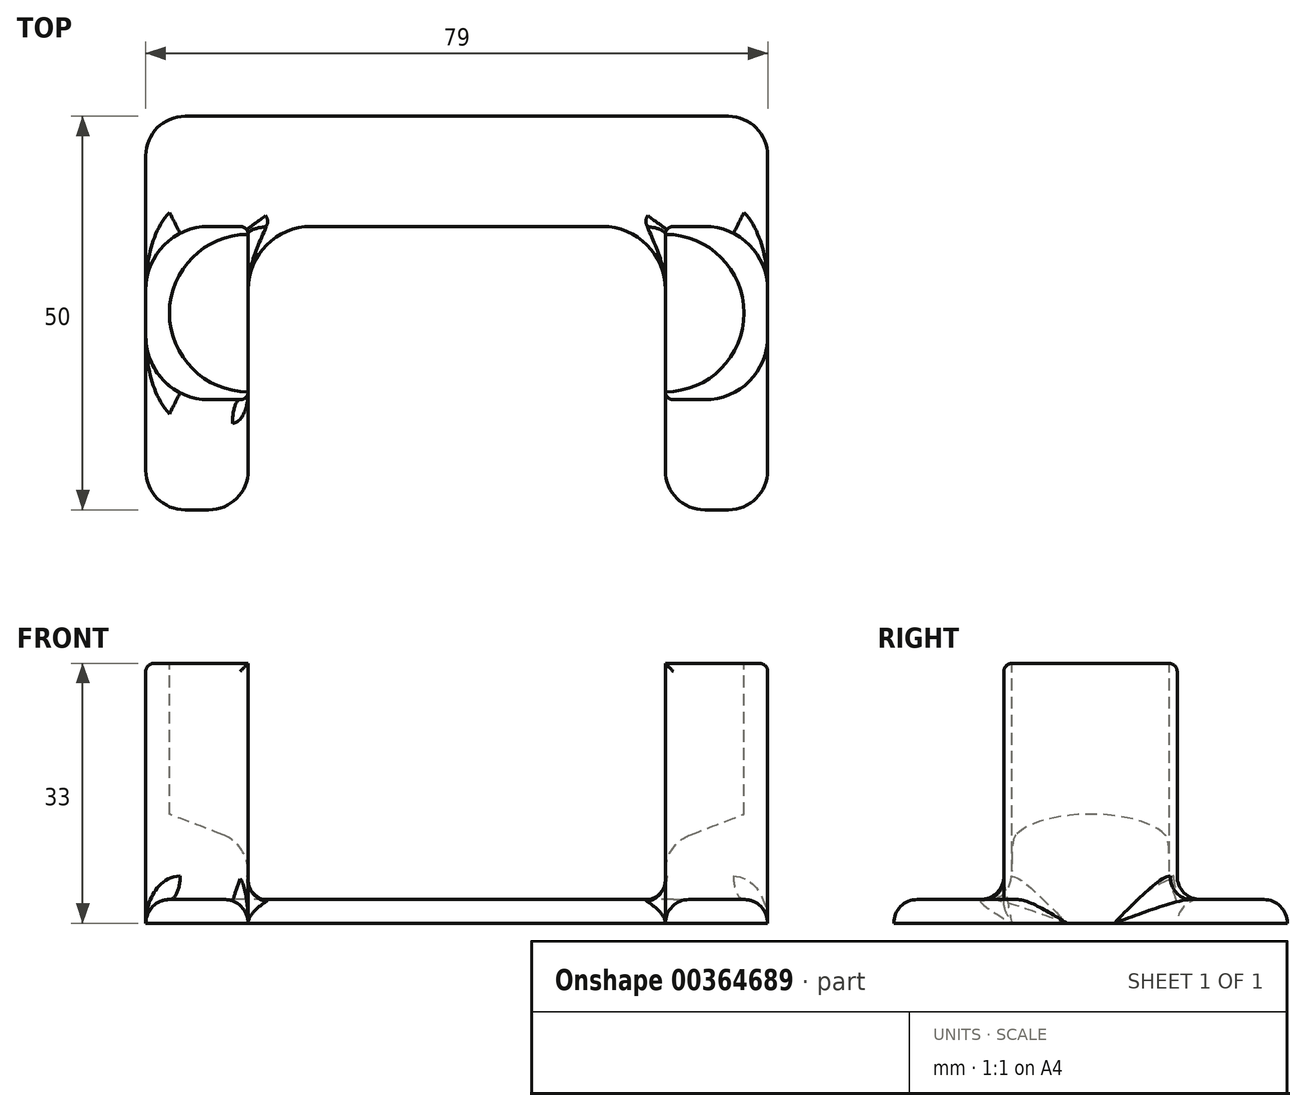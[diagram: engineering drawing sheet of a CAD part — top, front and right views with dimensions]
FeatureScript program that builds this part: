
annotation { "Feature Type Name" : "Feature", "Feature Type Description" : "" }
export const myFeature = defineFeature(function(context is Context, id is Id, definition is map)
    precondition{}
    {
        {
            var Q0;
            Q0=qCreatedBy(makeId("Top.planeOp"),FACE);
            var sketch = newSketch(context, id + "F0", { "sketchPlane" : qUnion([Q0])});
            skLineSegment(sketch, "E0", {"start": v(-45.81, 54.11) * mm, "end": v(33.19, 54.11) * mm});
            skLineSegment(sketch, "E1", {"start": v(33.19, 54.11) * mm, "end": v(33.19, 4.11) * mm});
            skLineSegment(sketch, "E2", {"start": v(33.19, 4.11) * mm, "end": v(20.19, 4.11) * mm});
            skLineSegment(sketch, "E3", {"start": v(20.19, 4.11) * mm, "end": v(20.19, 40.11) * mm});
            skLineSegment(sketch, "E4", {"start": v(20.19, 40.11) * mm, "end": v(-32.81, 40.11) * mm});
            skLineSegment(sketch, "E5", {"start": v(-32.81, 40.11) * mm, "end": v(-32.81, 4.11) * mm});
            skLineSegment(sketch, "E6", {"start": v(-32.81, 4.11) * mm, "end": v(-45.81, 4.11) * mm});
            skLineSegment(sketch, "E7", {"start": v(-45.81, 4.11) * mm, "end": v(-45.81, 54.11) * mm});
            skSolve(sketch);
        }
        {
            var Q0;
            Q0=makeQuery(id+"F0.imprint","IMPRINT",FACE,{"disambiguationData":[TD([[makeQuery(id+"F0.imprint","IMPRINT",EDGE,{"derivedFrom":sQuery(id+"F0.wireOp",EDGE,"E0")}),-1.0]])]});
            extrude(context, id + "F1", {"entities" : qUnion([Q0]), "depth" : 3 * mm});
        }
        {
            var Q0;
            Q0=makeQuery(id+"F1.opExtrude","CAP_FACE",FACE,{"disambiguationData":[OSD([sQuery(id+"F0.wireOp",EDGE,"E0"),sQuery(id+"F0.wireOp",EDGE,"E1"),sQuery(id+"F0.wireOp",EDGE,"E2"),sQuery(id+"F0.wireOp",EDGE,"E3"),sQuery(id+"F0.wireOp",EDGE,"E4"),sQuery(id+"F0.wireOp",EDGE,"E5"),sQuery(id+"F0.wireOp",EDGE,"E6"),sQuery(id+"F0.wireOp",EDGE,"E7")])],"isStart":false});
            var sketch = newSketch(context, id + "F2", { "sketchPlane" : qUnion([Q0])});
            skLineSegment(sketch, "E8.bottom", {"start": v(-32.81, 40.11) * mm, "end": v(-45.81, 40.11) * mm});
            skLineSegment(sketch, "E8.top", {"start": v(-32.81, 18.11) * mm, "end": v(-45.81, 18.11) * mm});
            skLineSegment(sketch, "E8.left", {"start": v(-32.81, 40.11) * mm, "end": v(-32.81, 18.11) * mm});
            skLineSegment(sketch, "E8.right", {"start": v(-45.81, 40.11) * mm, "end": v(-45.81, 18.11) * mm});
            skLineSegment(sketch, "E9.bottom", {"start": v(20.19, 40.11) * mm, "end": v(33.19, 40.11) * mm});
            skLineSegment(sketch, "E9.top", {"start": v(20.19, 18.11) * mm, "end": v(33.19, 18.11) * mm});
            skLineSegment(sketch, "E9.left", {"start": v(20.19, 40.11) * mm, "end": v(20.19, 18.11) * mm});
            skLineSegment(sketch, "E9.right", {"start": v(33.19, 40.11) * mm, "end": v(33.19, 18.11) * mm});
            skSolve(sketch);
        }
        {
            var Q0;
            Q0=makeQuery(id+"F2.imprint","IMPRINT",FACE,{"disambiguationData":[TD([[makeQuery(id+"F2.imprint","IMPRINT",EDGE,{"derivedFrom":sQuery(id+"F2.wireOp",EDGE,"E8.bottom")}),1.0]])]});
            var Q1;
            Q1=makeQuery(id+"F2.imprint","IMPRINT",FACE,{"disambiguationData":[TD([[makeQuery(id+"F2.imprint","IMPRINT",EDGE,{"derivedFrom":sQuery(id+"F2.wireOp",EDGE,"E9.bottom")}),-1.0]])]});
            extrude(context, id + "F3", {"entities" : qUnion([Q0, Q1]), "operationType" : NewBodyOperationType.ADD, "depth" : 30 * mm});
        }
        {
            var Q0;
            Q0=makeQuery(id+"F3.opExtrude","CAP_FACE",FACE,{"disambiguationData":[OSD([sQuery(id+"F2.wireOp",EDGE,"E8.bottom"),sQuery(id+"F2.wireOp",EDGE,"E8.top"),sQuery(id+"F2.wireOp",EDGE,"E8.left"),sQuery(id+"F2.wireOp",EDGE,"E8.right")])],"isStart":false});
            var sketch = newSketch(context, id + "F4", { "sketchPlane" : qUnion([Q0])});
            skCircle(sketch, "E10", {"center": v(-32.81, 29.11) * mm, "radius": 10 * mm});
            skSolve(sketch);
        }
        {
            var Q0;
            {var subQ0=sQuery(id+"F4.wireOp",EDGE,"E10");var subQ1=makeQuery(id+"F3.opExtrude","CAP_EDGE",EDGE,{"disambiguationData":[OSD([sQuery(id+"F2.wireOp",EDGE,"E8.left")])],"isStart":false});var subQ2=makeQuery(id+"F4.imprint","INTERSECT",VERTEX,{"disambiguationData":[OD(0.0)],"derivedFrom":[subQ1,subQ0]});Q0=makeQuery(id+"F4.imprint","IMPRINT",FACE,{"disambiguationData":[TD([[makeQuery(id+"F4.imprint","IMPRINT",EDGE,{"disambiguationData":[TD([[subQ2,-1.0]])],"derivedFrom":subQ0}),1.0]])]});}
            extrude(context, id + "F5", {"entities" : qUnion([Q0]), "operationType" : NewBodyOperationType.REMOVE, "oppositeDirection" : true, "depth" : 30 * mm});
        }
        {
            var Q0;
            Q0=makeQuery(id+"F3.opExtrude","CAP_FACE",FACE,{"disambiguationData":[OSD([sQuery(id+"F2.wireOp",EDGE,"E9.bottom"),sQuery(id+"F2.wireOp",EDGE,"E9.top"),sQuery(id+"F2.wireOp",EDGE,"E9.left"),sQuery(id+"F2.wireOp",EDGE,"E9.right")])],"isStart":false});
            var sketch = newSketch(context, id + "F6", { "sketchPlane" : qUnion([Q0])});
            skCircle(sketch, "E11", {"center": v(20.19, 29.11) * mm, "radius": 10 * mm});
            skSolve(sketch);
        }
        {
            var Q0;
            {var subQ0=sQuery(id+"F6.wireOp",EDGE,"E11");var subQ1=makeQuery(id+"F3.opExtrude","CAP_EDGE",EDGE,{"disambiguationData":[OSD([sQuery(id+"F2.wireOp",EDGE,"E9.left")])],"isStart":false});var subQ2=makeQuery(id+"F6.imprint","INTERSECT",VERTEX,{"disambiguationData":[OD(0.0)],"derivedFrom":[subQ1,subQ0]});Q0=makeQuery(id+"F6.imprint","IMPRINT",FACE,{"disambiguationData":[TD([[makeQuery(id+"F6.imprint","IMPRINT",EDGE,{"disambiguationData":[TD([[subQ2,1.0]])],"derivedFrom":subQ0}),1.0]])]});}
            extrude(context, id + "F7", {"entities" : qUnion([Q0]), "operationType" : NewBodyOperationType.REMOVE, "oppositeDirection" : true, "depth" : 30 * mm});
        }
        {
            var Q0;
            Q0=makeQuery(id+"F3.opExtrude","SWEPT_FACE",FACE,{"disambiguationData":[OSD([sQuery(id+"F2.wireOp",EDGE,"E8.top")])]});
            var sketch = newSketch(context, id + "F8", { "sketchPlane" : qUnion([Q0])});
            skLineSegment(sketch, "E12", {"start": v(-45.81, 3) * mm, "end": v(-45.81, 15) * mm});
            skLineSegment(sketch, "E13", {"start": v(-45.81, 15) * mm, "end": v(-32.81, 10) * mm});
            skLineSegment(sketch, "E14", {"start": v(-32.81, 10) * mm, "end": v(-32.81, 3) * mm});
            skLineSegment(sketch, "E15", {"start": v(-32.81, 3) * mm, "end": v(-45.81, 3) * mm});
            skSolve(sketch);
        }
        {
            var Q0;
            Q0=makeQuery(id+"F8.imprint","IMPRINT",FACE,{"disambiguationData":[TD([[makeQuery(id+"F8.imprint","IMPRINT",EDGE,{"derivedFrom":sQuery(id+"F8.wireOp",EDGE,"E12")}),1.0]])]});
            extrude(context, id + "F9", {"entities" : qUnion([Q0]), "operationType" : NewBodyOperationType.ADD, "depth" : -22 * mm});
        }
        {
            var Q0;
            Q0=makeQuery(id+"F3.opExtrude","SWEPT_FACE",FACE,{"disambiguationData":[OSD([sQuery(id+"F2.wireOp",EDGE,"E9.top")])]});
            var sketch = newSketch(context, id + "F10", { "sketchPlane" : qUnion([Q0])});
            skLineSegment(sketch, "E16", {"start": v(20.19, 3) * mm, "end": v(20.19, 10) * mm});
            skLineSegment(sketch, "E17", {"start": v(20.19, 10) * mm, "end": v(33.19, 15) * mm});
            skLineSegment(sketch, "E18", {"start": v(33.19, 15) * mm, "end": v(33.19, 3) * mm});
            skLineSegment(sketch, "E19", {"start": v(33.19, 3) * mm, "end": v(20.19, 3) * mm});
            skSolve(sketch);
        }
        {
            var Q0;
            Q0=makeQuery(id+"F10.imprint","IMPRINT",FACE,{"disambiguationData":[TD([[makeQuery(id+"F10.imprint","IMPRINT",EDGE,{"derivedFrom":sQuery(id+"F10.wireOp",EDGE,"E16")}),1.0]])]});
            extrude(context, id + "F11", {"entities" : qUnion([Q0]), "operationType" : NewBodyOperationType.ADD, "depth" : -22 * mm});
        }
        {
            var Q0;
            Q0=makeQuery(id+"F3.opExtrude","SWEPT_EDGE",EDGE,{"disambiguationData":[OSD([sQuery(id+"F0.wireOp",EDGE,"E1"),sQuery(id+"F2.wireOp",EDGE,"E9.top"),sQuery(id+"F2.wireOp",EDGE,"E9.right")])]});
            var Q1;
            Q1=makeQuery(id+"F3.opExtrude","SWEPT_EDGE",EDGE,{"disambiguationData":[OSD([sQuery(id+"F0.wireOp",EDGE,"E1"),sQuery(id+"F2.wireOp",EDGE,"E9.bottom"),sQuery(id+"F2.wireOp",EDGE,"E9.right")])]});
            var Q2;
            Q2=makeQuery(id+"F3.opExtrude","SWEPT_EDGE",EDGE,{"disambiguationData":[OSD([sQuery(id+"F0.wireOp",EDGE,"E7"),sQuery(id+"F2.wireOp",EDGE,"E8.top"),sQuery(id+"F2.wireOp",EDGE,"E8.right")])]});
            var Q3;
            Q3=makeQuery(id+"F3.opExtrude","SWEPT_EDGE",EDGE,{"disambiguationData":[OSD([sQuery(id+"F0.wireOp",EDGE,"E7"),sQuery(id+"F2.wireOp",EDGE,"E8.bottom"),sQuery(id+"F2.wireOp",EDGE,"E8.right")])]});
            fillet(context, id + "F12", {"entities" : qUnion([Q0, Q1, Q2, Q3]), "radius" : 8 * mm, "tangentPropagation" : true, "allowEdgeOverflow" : false});
        }
        {
            var Q0;
            Q0=makeQuery(id+"F9.opExtrude","SWEPT_EDGE",EDGE,{"disambiguationData":[OSD([sQuery(id+"F0.wireOp",EDGE,"E5"),sQuery(id+"F2.wireOp",EDGE,"E8.top"),sQuery(id+"F2.wireOp",EDGE,"E8.left"),sQuery(id+"F8.wireOp",EDGE,"E13"),sQuery(id+"F8.wireOp",EDGE,"E14")])]});
            var Q1;
            Q1=makeQuery(id+"F11.opExtrude","SWEPT_EDGE",EDGE,{"disambiguationData":[OSD([sQuery(id+"F0.wireOp",EDGE,"E3"),sQuery(id+"F2.wireOp",EDGE,"E9.top"),sQuery(id+"F2.wireOp",EDGE,"E9.left"),sQuery(id+"F10.wireOp",EDGE,"E16"),sQuery(id+"F10.wireOp",EDGE,"E17")])]});
            fillet(context, id + "F13", {"entities" : qUnion([Q0, Q1]), "radius" : 5 * mm, "tangentPropagation" : true, "allowEdgeOverflow" : false});
        }
        {
            var Q0;
            Q0=makeQuery(id+"F1.opExtrude","SWEPT_EDGE",EDGE,{"disambiguationData":[OSD([sQuery(id+"F0.wireOp",EDGE,"E4"),sQuery(id+"F0.wireOp",EDGE,"E5")])]});
            var Q1;
            Q1=makeQuery(id+"F1.opExtrude","SWEPT_EDGE",EDGE,{"disambiguationData":[OSD([sQuery(id+"F0.wireOp",EDGE,"E3"),sQuery(id+"F0.wireOp",EDGE,"E4")])]});
            fillet(context, id + "F14", {"entities" : qUnion([Q0, Q1]), "radius" : 8 * mm, "tangentPropagation" : true, "allowEdgeOverflow" : false});
        }
        {
            var Q0;
            Q0=makeQuery(id+"F1.opExtrude","SWEPT_EDGE",EDGE,{"disambiguationData":[OSD([sQuery(id+"F0.wireOp",EDGE,"E6"),sQuery(id+"F0.wireOp",EDGE,"E7")])]});
            var Q1;
            Q1=makeQuery(id+"F1.opExtrude","SWEPT_EDGE",EDGE,{"disambiguationData":[OSD([sQuery(id+"F0.wireOp",EDGE,"E5"),sQuery(id+"F0.wireOp",EDGE,"E6")])]});
            var Q2;
            Q2=makeQuery(id+"F1.opExtrude","SWEPT_EDGE",EDGE,{"disambiguationData":[OSD([sQuery(id+"F0.wireOp",EDGE,"E2"),sQuery(id+"F0.wireOp",EDGE,"E3")])]});
            var Q3;
            Q3=makeQuery(id+"F1.opExtrude","SWEPT_EDGE",EDGE,{"disambiguationData":[OSD([sQuery(id+"F0.wireOp",EDGE,"E1"),sQuery(id+"F0.wireOp",EDGE,"E2")])]});
            var Q4;
            Q4=makeQuery(id+"F1.opExtrude","SWEPT_EDGE",EDGE,{"disambiguationData":[OSD([sQuery(id+"F0.wireOp",EDGE,"E0"),sQuery(id+"F0.wireOp",EDGE,"E7")])]});
            var Q5;
            Q5=makeQuery(id+"F1.opExtrude","SWEPT_EDGE",EDGE,{"disambiguationData":[OSD([sQuery(id+"F0.wireOp",EDGE,"E0"),sQuery(id+"F0.wireOp",EDGE,"E1")])]});
            fillet(context, id + "F15", {"entities" : qUnion([Q0, Q1, Q2, Q3, Q4, Q5]), "radius" : 5 * mm, "tangentPropagation" : true, "allowEdgeOverflow" : false});
        }
        {
            var Q0;
            Q0=makeQuery(id+"F1.opExtrude","CAP_EDGE",EDGE,{"disambiguationData":[OSD([sQuery(id+"F0.wireOp",EDGE,"E0")])],"isStart":false});
            var Q1;
            Q1=makeQuery(id+"F1.opExtrude","CAP_EDGE",EDGE,{"disambiguationData":[OSD([sQuery(id+"F0.wireOp",EDGE,"E4")])],"isStart":false});
            var Q2;
            Q2=makeQuery(id+"F1.opExtrude","CAP_EDGE",EDGE,{"disambiguationData":[OSD([sQuery(id+"F0.wireOp",EDGE,"E6")])],"isStart":false});
            var Q3;
            Q3=makeQuery(id+"F1.opExtrude","CAP_EDGE",EDGE,{"disambiguationData":[OSD([sQuery(id+"F0.wireOp",EDGE,"E2")])],"isStart":false});
            fillet(context, id + "F16", {"entities" : qUnion([Q0, Q1, Q2, Q3]), "radius" : 3 * mm, "tangentPropagation" : true, "allowEdgeOverflow" : false});
        }
        {
            var Q0;
            Q0=makeQuery(id+"F3.opExtrude","SWEPT_EDGE",EDGE,{"disambiguationData":[OSD([sQuery(id+"F0.wireOp",EDGE,"E5"),sQuery(id+"F2.wireOp",EDGE,"E8.top"),sQuery(id+"F2.wireOp",EDGE,"E8.left")])]});
            var Q1;
            Q1=makeQuery(id+"F3.opExtrude","SWEPT_EDGE",EDGE,{"disambiguationData":[OSD([sQuery(id+"F0.wireOp",EDGE,"E4"),sQuery(id+"F2.wireOp",EDGE,"E8.bottom"),sQuery(id+"F2.wireOp",EDGE,"E8.left")])]});
            var Q2;
            Q2=makeQuery(id+"F3.opExtrude","SWEPT_EDGE",EDGE,{"disambiguationData":[OSD([sQuery(id+"F0.wireOp",EDGE,"E4"),sQuery(id+"F2.wireOp",EDGE,"E9.bottom"),sQuery(id+"F2.wireOp",EDGE,"E9.left")])]});
            var Q3;
            Q3=makeQuery(id+"F3.opExtrude","SWEPT_EDGE",EDGE,{"disambiguationData":[OSD([sQuery(id+"F0.wireOp",EDGE,"E3"),sQuery(id+"F2.wireOp",EDGE,"E9.top"),sQuery(id+"F2.wireOp",EDGE,"E9.left")])]});
            fillet(context, id + "F17", {"entities" : qUnion([Q0, Q1, Q2, Q3]), "radius" : 1 * mm, "tangentPropagation" : true, "allowEdgeOverflow" : false});
        }
        {
            var Q0;
            Q0=makeQuery(id+"F3.opExtrude","CAP_EDGE",EDGE,{"disambiguationData":[OSD([sQuery(id+"F2.wireOp",EDGE,"E8.right")])],"isStart":false});
            var Q1;
            Q1=makeQuery(id+"F3.opExtrude","CAP_EDGE",EDGE,{"disambiguationData":[OSD([sQuery(id+"F2.wireOp",EDGE,"E9.right")])],"isStart":false});
            fillet(context, id + "F18", {"entities" : qUnion([Q0, Q1]), "radius" : 1 * mm, "tangentPropagation" : true, "allowEdgeOverflow" : false});
        }
        {
            var Q0;
            Q0=makeQuery(id+"F3.opExtrude","CAP_EDGE",EDGE,{"disambiguationData":[OSD([sQuery(id+"F2.wireOp",EDGE,"E9.bottom")])],"isStart":true});
            var Q1;
            Q1=makeQuery(id+"F3.opExtrude","CAP_EDGE",EDGE,{"disambiguationData":[OSD([sQuery(id+"F2.wireOp",EDGE,"E8.bottom")])],"isStart":true});
            var Q2;
            Q2=makeQuery(id+"F3.opExtrude","CAP_EDGE",EDGE,{"disambiguationData":[OSD([sQuery(id+"F2.wireOp",EDGE,"E9.top")])],"isStart":true});
            var Q3;
            Q3=makeQuery(id+"F3.opExtrude","CAP_EDGE",EDGE,{"disambiguationData":[OSD([sQuery(id+"F2.wireOp",EDGE,"E8.top")])],"isStart":true});
            fillet(context, id + "F19", {"entities" : qUnion([Q0, Q1, Q2, Q3]), "radius" : 3 * mm, "tangentPropagation" : true, "allowEdgeOverflow" : false});
        }
    });
